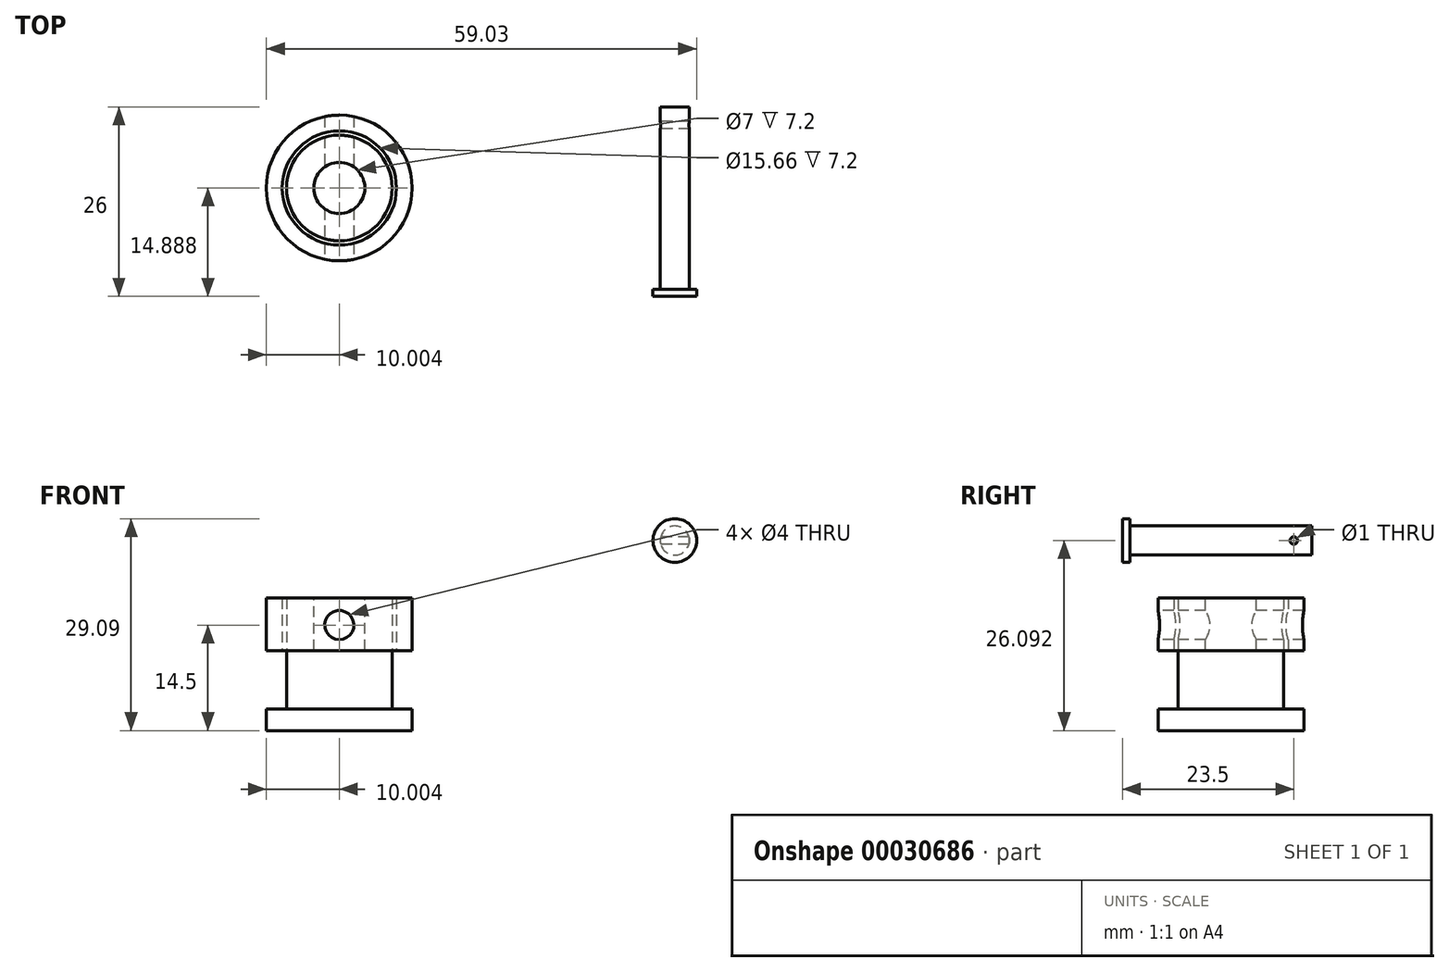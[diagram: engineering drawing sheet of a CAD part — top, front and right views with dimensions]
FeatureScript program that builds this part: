
annotation { "Feature Type Name" : "Feature", "Feature Type Description" : "" }
export const myFeature = defineFeature(function(context is Context, id is Id, definition is map)
    precondition{}
    {
        {
            var Q0;
            Q0=qCreatedBy(makeId("Top.planeOp"),FACE);
            var sketch = newSketch(context, id + "F0", { "sketchPlane" : qUnion([Q0])});
            skCircle(sketch, "E0", {"center": v(-31.7, 83.89) * mm, "radius": 10 * mm});
            skCircle(sketch, "E1", {"center": v(-31.7, 83.89) * mm, "radius": 7.83 * mm});
            skSolve(sketch);
        }
        {
            var Q0;
            Q0=qSketchRegion(id+"F0",true);
            var Q1;
            Q1=makeQuery(id+"F0.imprint","IMPRINT",FACE,{"disambiguationData":[TD([[makeQuery(id+"F0.imprint","IMPRINT",EDGE,{"derivedFrom":sQuery(id+"F0.wireOp",EDGE,"E0")}),1.0]])]});
            extrude(context, id + "F1", {"entities" : qUnion([Q0, Q1]), "depth" : 7 * mm, "hasSecondDirection" : true, "secondDirectionOppositeDirection" : true, "secondDirectionDepth" : .2 * mm});
        }
        {
            var Q0;
            Q0=qCreatedBy(makeId("Front.planeOp"),FACE);
            var sketch = newSketch(context, id + "F2", { "sketchPlane" : qUnion([Q0])});
            skCircle(sketch, "E2", {"center": v(-31.7, 3.3) * mm, "radius": 2 * mm});
            skLineSegment(sketch, "E3.0", {"start": v(-41.7, 7) * mm, "end": v(-21.7, 7) * mm});
            skLineSegment(sketch, "E4", {"start": v(-41.7, 0) * mm, "end": v(-41.7, 7) * mm});
            skLineSegment(sketch, "E5", {"start": v(-21.7, 7) * mm, "end": v(-21.7, 0) * mm});
            skSolve(sketch);
        }
        {
            var Q0;
            Q0=makeQuery(id+"F1.opExtrude","CAP_FACE",FACE,{"disambiguationData":[OSD([sQuery(id+"F0.wireOp",EDGE,"E0"),sQuery(id+"F0.wireOp",EDGE,"E1")])],"isStart":true});
            var sketch = newSketch(context, id + "F3", { "sketchPlane" : qUnion([Q0])});
            skCircle(sketch, "E6.0", {"center": v(-31.7, -83.89) * mm, "radius": 7.83 * mm});
            skCircle(sketch, "E7.0", {"center": v(-31.7, -83.89) * mm, "radius": 10 * mm});
            skCircle(sketch, "E8.0", {"center": v(-31.7, -83.89) * mm, "radius": 7.25 * mm});
            skSolve(sketch);
        }
        {
            var Q0;
            Q0=makeQuery(id+"F3.imprint","IMPRINT",FACE,{"disambiguationData":[TD([[makeQuery(id+"F3.imprint","IMPRINT",EDGE,{"derivedFrom":sQuery(id+"F3.wireOp",EDGE,"E8.0")}),1.0]])]});
            var Q1;
            Q1=makeQuery(id+"F1.opExtrude","CAP_FACE",FACE,{"disambiguationData":[OSD([sQuery(id+"F0.wireOp",EDGE,"E0"),sQuery(id+"F0.wireOp",EDGE,"E1")])],"isStart":false});
            extrude(context, id + "F4", {"entities" : qUnion([Q0]), "endBound" : BoundingType.UP_TO_SURFACE, "oppositeDirection" : true, "endBoundEntityFace" : qUnion([Q1]), "depth" : 25 * mm, "hasSecondDirection" : true, "secondDirectionOppositeDirection" : false, "secondDirectionDepth" : 8 * mm});
        }
        {
            var Q0;
            Q0=makeQuery(id+"F3.imprint","IMPRINT",FACE,{"disambiguationData":[TD([[makeQuery(id+"F3.imprint","IMPRINT",EDGE,{"derivedFrom":sQuery(id+"F3.wireOp",EDGE,"E6.0")}),-1.0]])]});
            var Q1;
            Q1=makeQuery(id+"F3.imprint","IMPRINT",FACE,{"disambiguationData":[TD([[makeQuery(id+"F3.imprint","IMPRINT",EDGE,{"derivedFrom":sQuery(id+"F3.wireOp",EDGE,"E6.0")}),1.0]])]});
            var Q2;
            Q2=makeQuery(id+"F3.imprint","IMPRINT",FACE,{"disambiguationData":[TD([[makeQuery(id+"F3.imprint","IMPRINT",EDGE,{"derivedFrom":sQuery(id+"F3.wireOp",EDGE,"E8.0")}),1.0]])]});
            extrude(context, id + "F5", {"entities" : qUnion([Q0, Q1, Q2]), "operationType" : NewBodyOperationType.ADD, "depth" : 11 * mm, "hasSecondDirection" : true, "secondDirectionOppositeDirection" : false, "secondDirectionDepth" : 8 * mm});
        }
        {
            var Q0;
            Q0=qCreatedBy(makeId("Front.planeOp"),FACE);
            cPlane(context, id + "F6", {"entities" : qUnion([Q0]), "cplaneType" : CPlaneType.OFFSET, "offset" : 70 * mm, "oppositeDirection" : true, "width" : 150 * mm, "height" : 150 * mm});
        }
        {
            var Q0;
            Q0=qCreatedBy(id+"F6.planeOp",FACE);
            var sketch = newSketch(context, id + "F7", { "sketchPlane" : qUnion([Q0])});
            skCircle(sketch, "E9", {"center": v(14.33, 14.9) * mm, "radius": 2 * mm});
            skCircle(sketch, "E10", {"center": v(14.33, 14.9) * mm, "radius": 3 * mm});
            skSolve(sketch);
        }
        {
            var Q0;
            Q0=makeQuery(id+"F1.opExtrude","CAP_FACE",FACE,{"disambiguationData":[OSD([sQuery(id+"F0.wireOp",EDGE,"E0"),sQuery(id+"F0.wireOp",EDGE,"E1")])],"isStart":false});
            var sketch = newSketch(context, id + "F8", { "sketchPlane" : qUnion([Q0])});
            skCircle(sketch, "E11", {"center": v(-31.7, 83.89) * mm, "radius": 3.5 * mm});
            skSolve(sketch);
        }
        {
            var Q0;
            Q0=makeQuery(id+"F8.imprint","IMPRINT",FACE,{"disambiguationData":[TD([[makeQuery(id+"F8.imprint","IMPRINT",EDGE,{"derivedFrom":sQuery(id+"F8.wireOp",EDGE,"E11")}),1.0]])]});
            var Q1;
            Q1=makeQuery(id+"F1.opExtrude","CAP_FACE",FACE,{"disambiguationData":[OSD([sQuery(id+"F0.wireOp",EDGE,"E0"),sQuery(id+"F0.wireOp",EDGE,"E1")])],"isStart":true});
            extrude(context, id + "F9", {"entities" : qUnion([Q0]), "operationType" : NewBodyOperationType.REMOVE, "endBound" : BoundingType.UP_TO_SURFACE, "oppositeDirection" : true, "endBoundEntityFace" : qUnion([Q1]), "depth" : 3 * mm});
        }
        {
            var Q0;
            Q0=qSketchRegion(id+"F2",true);
            var Q1;
            Q1=makeQuery(id+"F2.imprint","IMPRINT",FACE,{"disambiguationData":[TD([[makeQuery(id+"F2.imprint","IMPRINT",EDGE,{"derivedFrom":sQuery(id+"F2.wireOp",EDGE,"E2")}),1.0]])]});
            extrude(context, id + "F10", {"entities" : qUnion([Q0, Q1]), "operationType" : NewBodyOperationType.REMOVE, "endBound" : BoundingType.THROUGH_ALL, "oppositeDirection" : true, "depth" : 25 * mm});
        }
        {
            var Q0;
            Q0=makeQuery(id+"F7.imprint","IMPRINT",FACE,{"disambiguationData":[TD([[makeQuery(id+"F7.imprint","IMPRINT",EDGE,{"derivedFrom":sQuery(id+"F7.wireOp",EDGE,"E9")}),1.0]])]});
            extrude(context, id + "F11", {"entities" : qUnion([Q0]), "oppositeDirection" : true, "depth" : 25 * mm});
        }
        {
            var Q0;
            Q0=makeQuery(id+"F7.imprint","IMPRINT",FACE,{"disambiguationData":[TD([[makeQuery(id+"F7.imprint","IMPRINT",EDGE,{"derivedFrom":sQuery(id+"F7.wireOp",EDGE,"E9")}),-1.0]])]});
            var Q1;
            Q1=makeQuery(id+"F7.imprint","IMPRINT",FACE,{"disambiguationData":[TD([[makeQuery(id+"F7.imprint","IMPRINT",EDGE,{"derivedFrom":sQuery(id+"F7.wireOp",EDGE,"E9")}),1.0]])]});
            extrude(context, id + "F12", {"entities" : qUnion([Q0, Q1]), "operationType" : NewBodyOperationType.ADD, "depth" : 1 * mm});
        }
        {
            var Q0;
            Q0=qCreatedBy(makeId("Right.planeOp"),FACE);
            var sketch = newSketch(context, id + "F13", { "sketchPlane" : qUnion([Q0])});
            skCircle(sketch, "E12", {"center": v(92.5, 14.9) * mm, "radius": 0.5 * mm});
            skLineSegment(sketch, "E13.0", {"start": v(95, 12.9) * mm, "end": v(95, 16.9) * mm});
            skSolve(sketch);
        }
        {
            var Q0;
            Q0=makeQuery(id+"F13.imprint","IMPRINT",FACE,{"disambiguationData":[TD([[makeQuery(id+"F13.imprint","IMPRINT",EDGE,{"derivedFrom":sQuery(id+"F13.wireOp",EDGE,"E12")}),1.0]])]});
            extrude(context, id + "F14", {"entities" : qUnion([Q0]), "operationType" : NewBodyOperationType.REMOVE, "depth" : 25 * mm});
        }
    });
